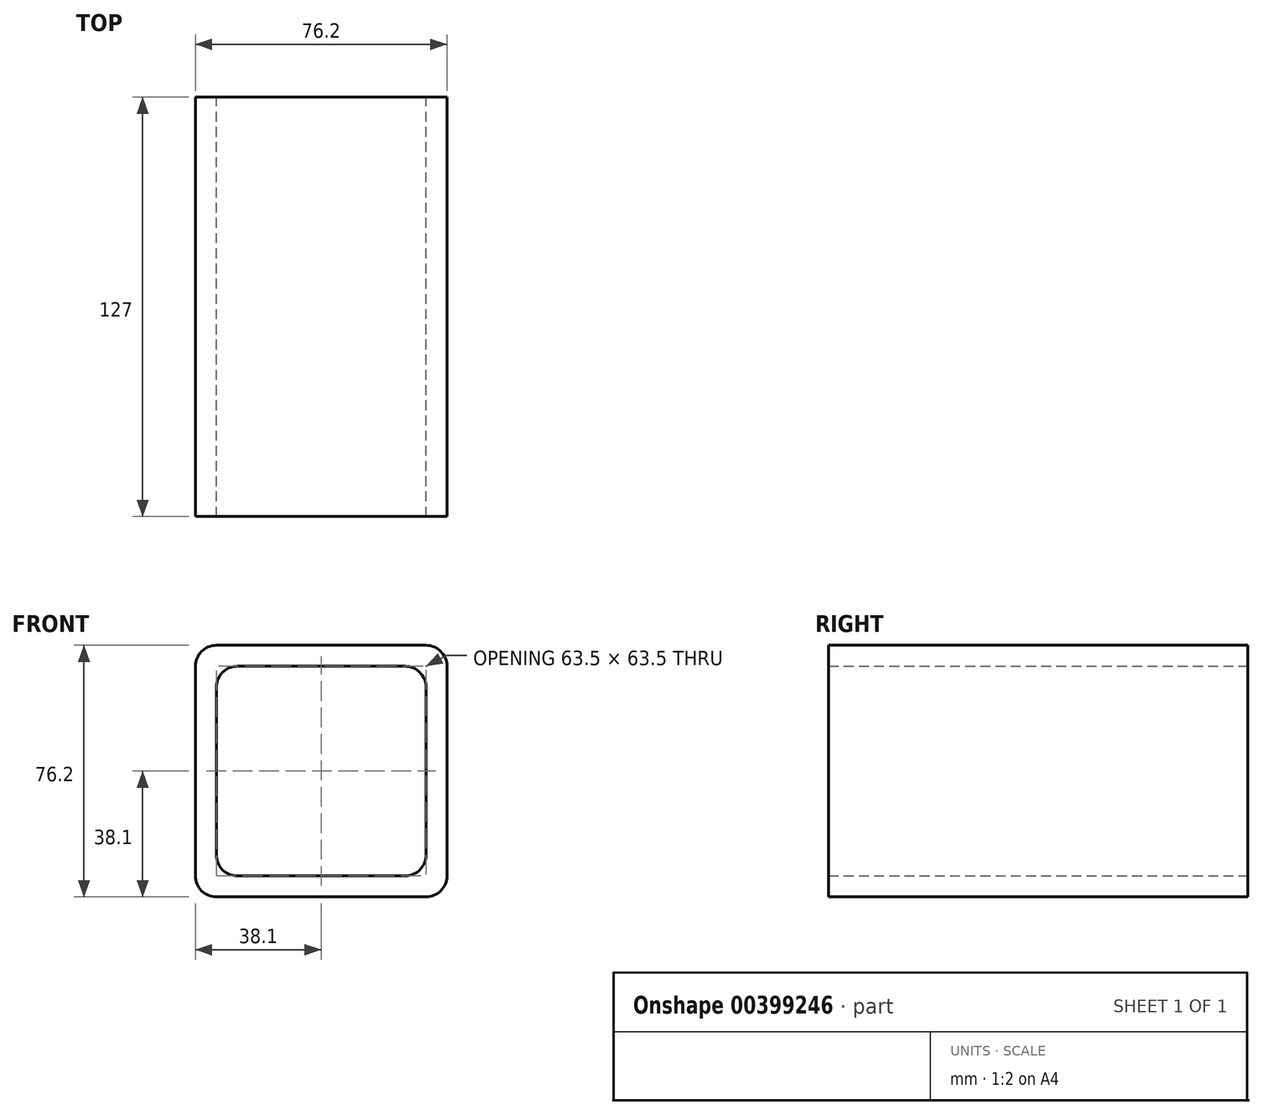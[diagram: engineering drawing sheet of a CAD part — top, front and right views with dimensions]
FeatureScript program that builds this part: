
annotation { "Feature Type Name" : "Feature", "Feature Type Description" : "" }
export const myFeature = defineFeature(function(context is Context, id is Id, definition is map)
    precondition{}
    {
        {
            var Q0;
            Q0=qCreatedBy(makeId("Front.planeOp"),FACE);
            var sketch = newSketch(context, id + "F0", { "sketchPlane" : qUnion([Q0])});
            skLineSegment(sketch, "E0.bottom", {"start": v(31.75, 38.1) * mm, "end": v(-31.75, 38.1) * mm});
            skLineSegment(sketch, "E0.top", {"start": v(31.75, -38.1) * mm, "end": v(-31.75, -38.1) * mm});
            skLineSegment(sketch, "E0.left", {"start": v(38.1, 31.75) * mm, "end": v(38.1, -31.75) * mm});
            skLineSegment(sketch, "E0.right", {"start": v(-38.1, 31.75) * mm, "end": v(-38.1, -31.75) * mm});
            skPoint(sketch, "E0.middle", {"position": v(0, 0) * mm});
            skPoint(sketch, "E1.visualSharp", {"position": v(38.1, 38.1) * mm});
            skArc(sketch, "E1.filletArc", {"start": v(38.1, 31.75) * mm, "mid": v(36.24, 36.24) * mm, "end": v(31.75, 38.1) * mm});
            skPoint(sketch, "E2.visualSharp", {"position": v(-38.1, 38.1) * mm});
            skArc(sketch, "E2.filletArc", {"start": v(-31.75, 38.1) * mm, "mid": v(-36.24, 36.24) * mm, "end": v(-38.1, 31.75) * mm});
            skPoint(sketch, "E3.visualSharp", {"position": v(-38.1, -38.1) * mm});
            skArc(sketch, "E3.filletArc", {"start": v(-38.1, -31.75) * mm, "mid": v(-36.24, -36.24) * mm, "end": v(-31.75, -38.1) * mm});
            skPoint(sketch, "E4.visualSharp", {"position": v(38.1, -38.1) * mm});
            skArc(sketch, "E4.filletArc", {"start": v(31.75, -38.1) * mm, "mid": v(36.24, -36.24) * mm, "end": v(38.1, -31.75) * mm});
            skLineSegment(sketch, "E5.0", {"start": v(-31.75, 25.4) * mm, "end": v(-31.75, -25.4) * mm});
            skLineSegment(sketch, "E5.1", {"start": v(25.4, 31.75) * mm, "end": v(-25.4, 31.75) * mm});
            skLineSegment(sketch, "E5.2", {"start": v(31.75, 25.4) * mm, "end": v(31.75, -25.4) * mm});
            skLineSegment(sketch, "E5.3", {"start": v(25.4, -31.75) * mm, "end": v(-25.4, -31.75) * mm});
            skArc(sketch, "E6.filletArc", {"start": v(-25.4, 31.75) * mm, "mid": v(-29.9, 29.9) * mm, "end": v(-31.75, 25.4) * mm});
            skArc(sketch, "E7.filletArc", {"start": v(31.75, 25.4) * mm, "mid": v(29.9, 29.9) * mm, "end": v(25.4, 31.75) * mm});
            skArc(sketch, "E8.filletArc", {"start": v(-31.75, -25.4) * mm, "mid": v(-29.9, -29.9) * mm, "end": v(-25.4, -31.75) * mm});
            skArc(sketch, "E9.filletArc", {"start": v(25.4, -31.75) * mm, "mid": v(29.9, -29.9) * mm, "end": v(31.75, -25.4) * mm});
            skSolve(sketch);
        }
        {
            var Q0;
            Q0 = qSketchRegion(id + "F0", true);
            extrude(context, id + "F1", {"entities" : qUnion([Q0]), "depth" : 127 * mm});
        }
    });
